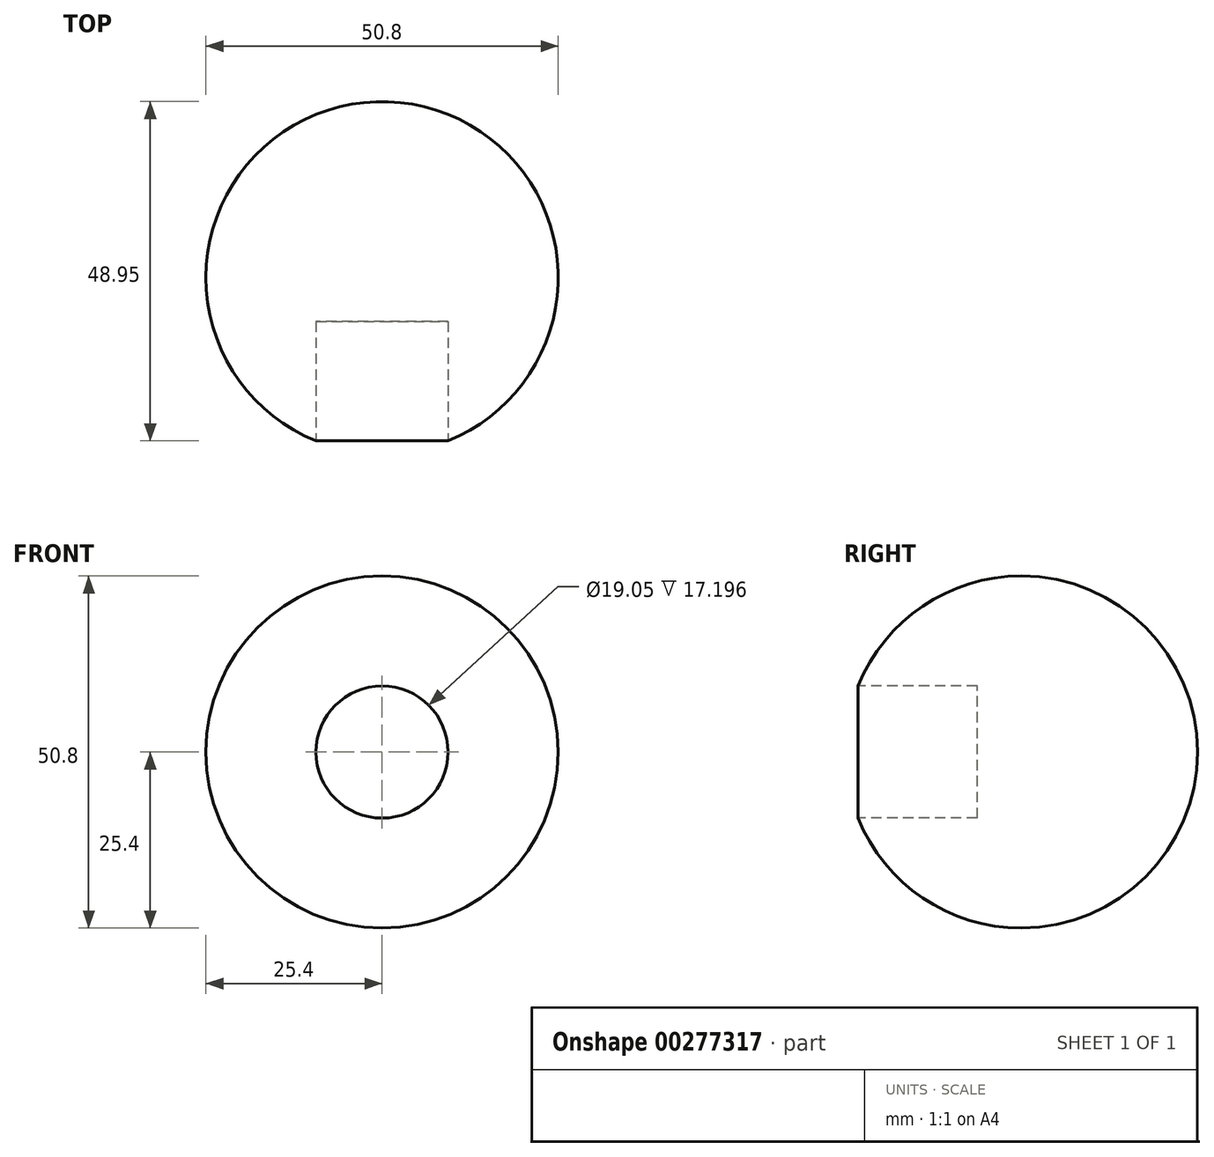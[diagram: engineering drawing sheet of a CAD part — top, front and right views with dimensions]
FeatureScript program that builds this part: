
annotation { "Feature Type Name" : "Feature", "Feature Type Description" : "" }
export const myFeature = defineFeature(function(context is Context, id is Id, definition is map)
    precondition{}
    {
        {
            var Q0;
            Q0=qCreatedBy(makeId("Front.planeOp"),FACE);
            var sketch = newSketch(context, id + "F0", { "sketchPlane" : qUnion([Q0])});
            skArc(sketch, "E0", {"start": v(0, -25.4) * mm, "mid": v(25.4, 0) * mm, "end": v(0, 25.4) * mm});
            skLineSegment(sketch, "E1", {"start": v(0, 25.4) * mm, "end": v(0, -25.4) * mm});
            skSolve(sketch);
        }
        {
            var Q0;
            Q0 = qSketchRegion(id + "F0", true);
            var Q1;
            Q1=sQuery(id+"F0.wireOp",EDGE,"E1");
            revolve(context, id + "F1", {"entities" : qUnion([Q0]), "axis" : qUnion([Q1]), "revolveType" : RevolveType.FULL});
        }
        {
            var Q0;
            Q0=qCreatedBy(makeId("Front.planeOp"),FACE);
            cPlane(context, id + "F2", {"entities" : qUnion([Q0]), "cplaneType" : CPlaneType.OFFSET, "offset" : 25.4 * mm, "width" : 152.4 * mm, "height" : 152.4 * mm});
        }
        {
            var Q0;
            Q0=qCreatedBy(id+"F2.planeOp",FACE);
            var sketch = newSketch(context, id + "F3", { "sketchPlane" : qUnion([Q0])});
            skPoint(sketch, "E2.0", {"position": v(0, 0) * mm});
            skCircle(sketch, "E3", {"center": v(0, 0) * mm, "radius": 9.53 * mm});
            skSolve(sketch);
        }
        {
            var Q0;
            Q0 = qSketchRegion(id + "F3", true);
            extrude(context, id + "F4", {"entities" : qUnion([Q0]), "operationType" : NewBodyOperationType.REMOVE, "oppositeDirection" : true, "depth" : 19.05 * mm});
        }
    });
